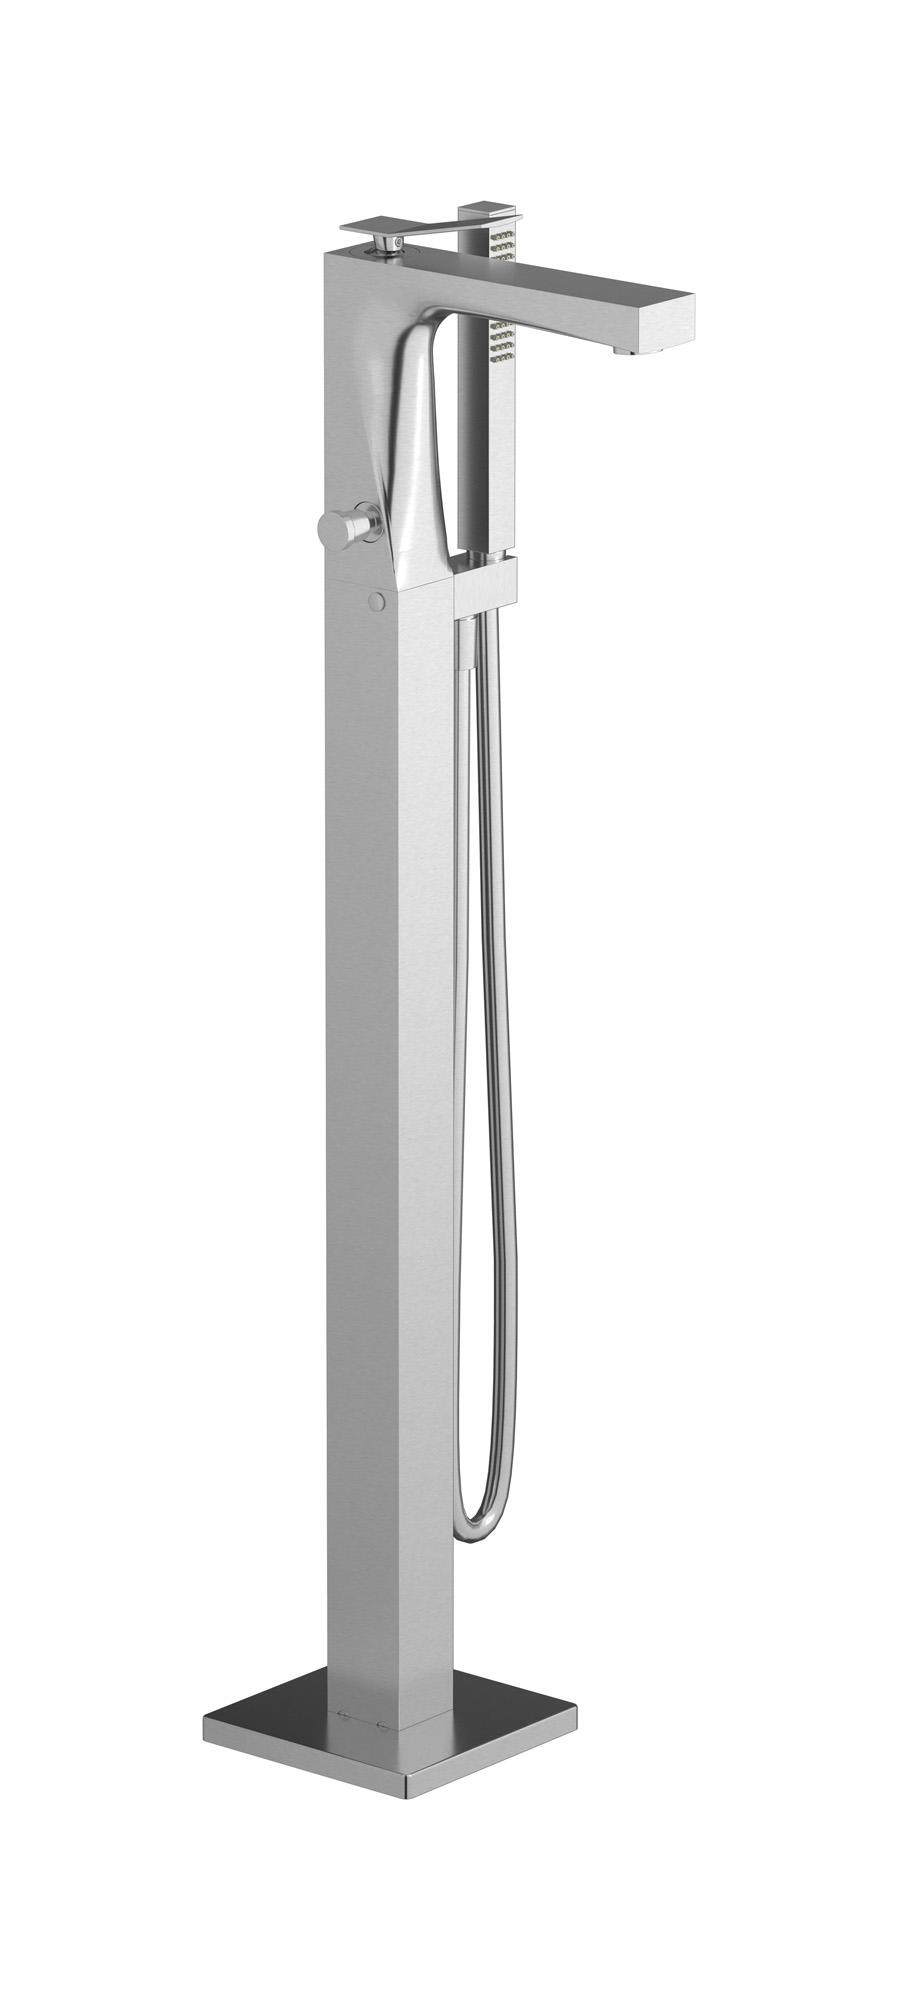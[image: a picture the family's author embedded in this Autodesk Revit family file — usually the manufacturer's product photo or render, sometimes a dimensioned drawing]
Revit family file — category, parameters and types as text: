
# Revit family: WA399
name_source: partatom
category: Apparecchi idraulici
units: mm (PartAtom-declared; Revit-internal decimal feet)

## family parameters
Basato su piano di lavoro = No
Condiviso = No
Mantieni orientamento annotazione = No
Numero OmniClass = 23.45.55.17
Punto di calcolo locali = No
Quota connettore circolare = Usa diametro
Sempre verticale = Sì
Taglio con vuoti quando caricato = No
Tipo di parte = Normale
Titolo OmniClass = Mixing Faucets

## types (12) — shared parameters
Cold water inlet = 10 mm  [stored 0.0328084 ft]
Commenti sul tipo = Freestanding bath filler
Connessione CW = No
Connessione HW = No
Connessione di scarico = No
Connessione di ventilazione = No
Descrizione = Freestanding bath filler
Hot water inlet = 10 mm  [stored 0.0328084 ft]
Produttore = IB Rubinetterie S.p.A.
URL = https://www.weareib.it
zero-valued in all types: Prospetto di default

## per-type parameters (varying)
| type | Finishes surface | Immagine tipo | Modello |
| Chrome | IB_Chrome | WA399CC.jpg | WA399CC |
| Brushed nickel | IB_Brushed nickel | WA399SS.jpg | WA399SS |
| Matt white | IB_matt white | WA399BO.jpg | WA399BO |
| Matt black | IB_matt black | WA399NP.jpg | WA399NP |
| Black chrome | IB_Black chrome | WA399CF.jpg | WA399CF |
| Brushed black chrome | IB_Brushed black chrome | WA399CS.jpg | WA399CS |
| Pale gold | IB_Pale gold | WA399II.jpg | WA399II |
| Brushed pale gold | IB_brushed pale gold | WA399IS.jpg | WA399IS |
| Rose gold | IB_Rose gold | WA399RS.jpg | WA399RS |
| Brushed rose gold | IB_Brushed rose gold | WA399SR.jpg | WA399SR |
| Gold | IB_gold | WA399OO.jpg | WA399OO |
| Brushed gold | IB_brushed gold | WA399OS.jpg | WA399OS |

note: [stored X ft] marks values corroborated as IEEE doubles in the binary element streams (Revit-internal decimal feet)
